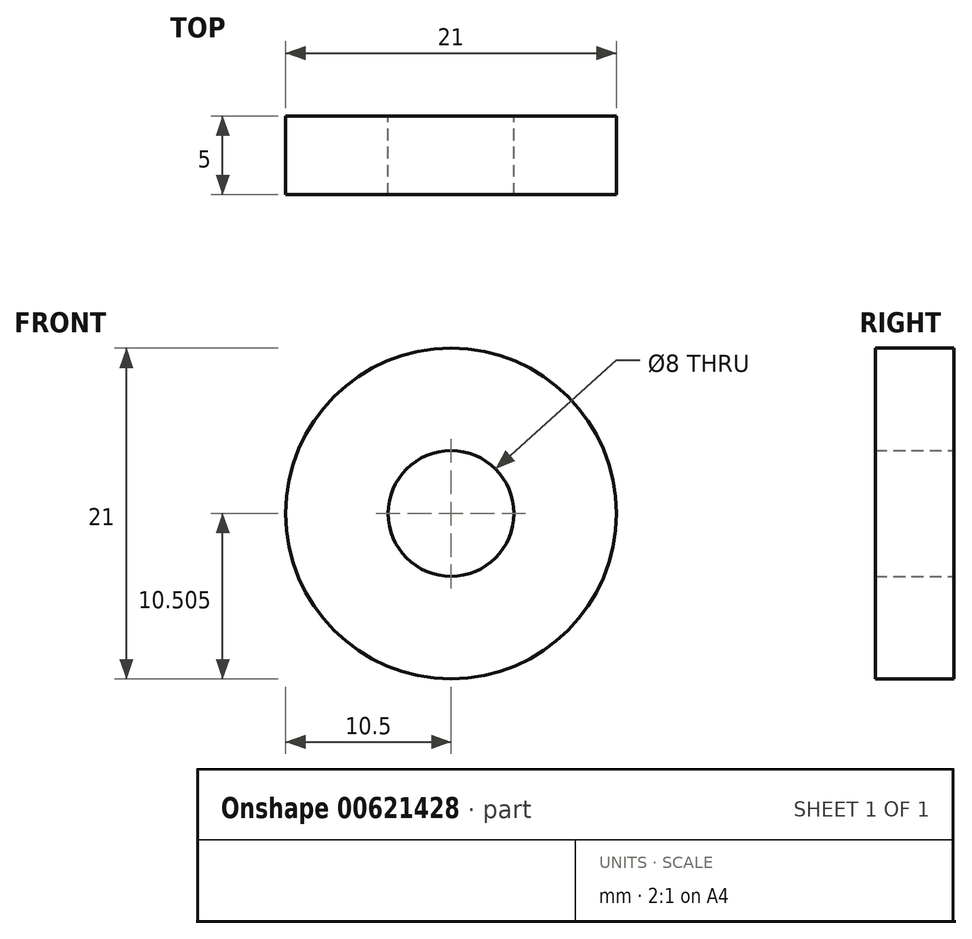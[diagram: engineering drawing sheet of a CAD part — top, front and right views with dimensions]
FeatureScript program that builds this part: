
annotation { "Feature Type Name" : "Feature", "Feature Type Description" : "" }
export const myFeature = defineFeature(function(context is Context, id is Id, definition is map)
    precondition{}
    {
        {
            var Q0;
            Q0=qCreatedBy(makeId("Front.planeOp"),FACE);
            var sketch = newSketch(context, id + "F0", { "sketchPlane" : qUnion([Q0])});
            skCircle(sketch, "E0", {"center": v(0, -1.68) * mm, "radius": 10.5 * mm});
            skCircle(sketch, "E1", {"center": v(0, -1.68) * mm, "radius": 4 * mm});
            skSolve(sketch);
        }
        {
            var Q0;
            Q0=makeQuery(id+"F0.imprint","IMPRINT",FACE,{"disambiguationData":[TD([[makeQuery(id+"F0.imprint","IMPRINT",EDGE,{"derivedFrom":sQuery(id+"F0.wireOp",EDGE,"E0")}),1.0]])]});
            extrude(context, id + "F1", {"entities" : qUnion([Q0]), "depth" : 5 * mm, "offsetDistance" : 25 * mm});
        }
    });
